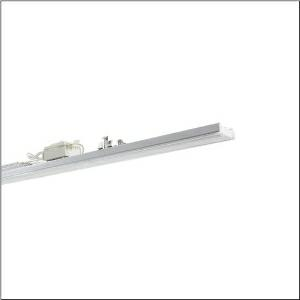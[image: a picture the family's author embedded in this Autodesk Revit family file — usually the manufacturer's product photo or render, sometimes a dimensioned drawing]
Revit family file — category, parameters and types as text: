
# Revit family: licross_r__11_recessed_tw_51tl12tnt9xx_ba8c
name_source: partatom
category: Lighting Fixtures
units: mm (PartAtom-declared; Revit-internal decimal feet)

## family parameters
Cut with Voids When Loaded = No
Host = Face
Light Source = No
Part Type = Normal
Room Calculation Point = No
Round Connector Dimension = Use Diameter
Shared = No

## types (1)
- --- (1 x LED 2700 K ... 6500 K, 9050 lm, 56 W, 2700K)
    Apparent Load = 56 VA
    CIE Flux Codes = 66 91 98 100 100
    Color Rendering = 80
    Color Temperature = 2700K
    Default Elevation = 1800 mm
    Description = Licross® 11 Recessed TW, luminaire insert, of sheet steel, galvanised, coil coated, white, length: 1.500mm, width: 66mm, height: 67mm, LED rated luminous flux: 9.050lm, light colour: 8tw, control gear: DALI DT8, with plug, 5-pole, with phase selection, mains connection: 220..240V, AC, 50/60Hz, rated input power: 56W, halogen-free wiring, primary optical cover: cover, of PMMA, light emission: direct distribution, primary light characteristic: symmetric, protection rating (complete): IP40, insulation class (complete): insulation class I (protective earthing), certification: CE, ENEC, VDE, UKCA, protection symbol: D if used in an environment without relevant dust loads with corresponding accessories, impact resistance: IK06, permissible ambient temperature for indoor applications: -25..+35°C, corresponds to IFS (International Featured Standards) requirements for safety and quality in the food industry, reducing of maximum allowable ambient temperature of 5°C with ceiling mounting, LABS conformity tested according to VDMA 24364:2018-05, packaging unit: 1 piece
    Height = 58 mm
    Lamp = 1 x LED 2700 K ... 6500 K
    Lamp Light Flux = 9050 lm
    Lamp Power = 56 W
    Lamp count = 1
    Length = 1500 mm
    Luminous efficacy = 162 lm/W
    Manufacturer = Siteco
    ModVariant = No
    Model = 51TL12TNT9XX
    Mounting Place = Ceiling
    Mounting Type = Pendant
    Number of Poles = 1
    OnlyDefault = Yes
    Power Factor = 1
    Product Name = Licross® 11 Recessed TW
    Product group = luminaire insert
    ProductGroupID = 902
    Protection Class = Protection class I
    Protection Degree = IP 40
    RLX_Detail_Level = 1
    RLX_Emergency_Light_Flux = 0 lm
    RLX_Emergency_Type = 0
    RLX_Emergency_Type_DB = No
    RlxData = <blob elided: 20797 chars, md5=01b9318f>
    Socket = socket
    Standby Power = 0 W
    System Light Flux = 9050 lm
    System Power = 56 W
    Type Comments = individual setting: CCT=2700K
    Type Image = l_1296930.jpg
    URL = http://relux.com
    VarID = @adj_048944
    Voltage = 0 V
    Weight = 0.00 kg
    Width = 66 mm

## geometry (parser evidence)
native form markers: Blend x4, Sweep x11
no freeform markers — native parametric forms only
